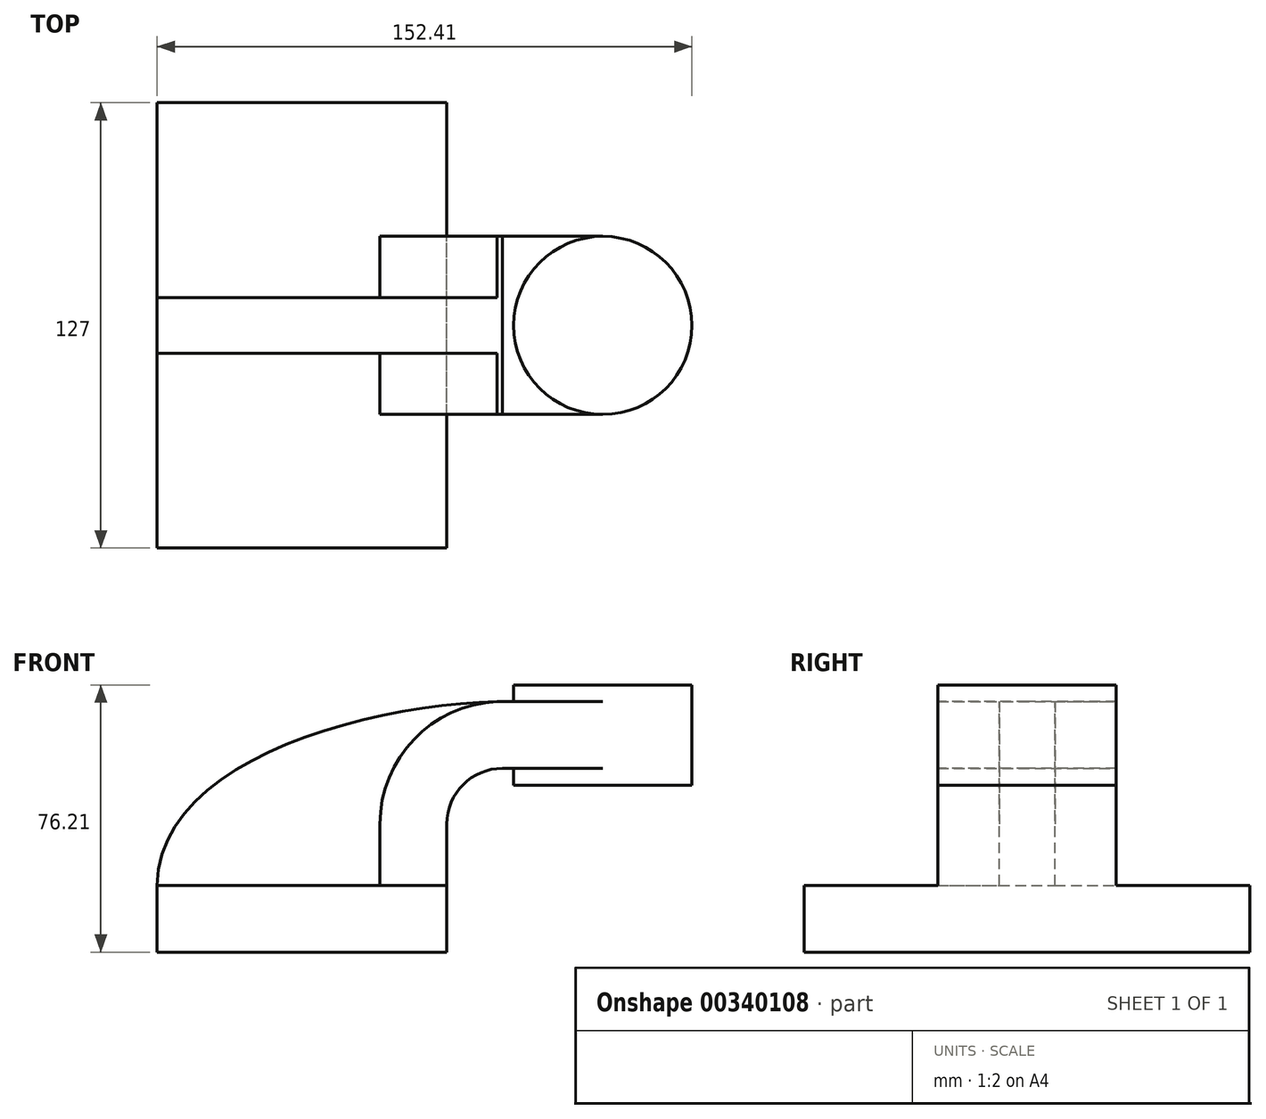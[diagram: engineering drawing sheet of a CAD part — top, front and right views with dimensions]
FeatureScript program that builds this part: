
annotation { "Feature Type Name" : "Feature", "Feature Type Description" : "" }
export const myFeature = defineFeature(function(context is Context, id is Id, definition is map)
    precondition{}
    {
        {
            var Q0;
            Q0=qCreatedBy(makeId("Front.planeOp"),FACE);
            var sketch = newSketch(context, id + "F0", { "sketchPlane" : qUnion([Q0])});
            skLineSegment(sketch, "E0.bottom", {"start": v(-41.28, -9.53) * mm, "end": v(41.28, -9.53) * mm});
            skLineSegment(sketch, "E0.top", {"start": v(-41.28, 9.52) * mm, "end": v(41.27, 9.52) * mm});
            skLineSegment(sketch, "E0.left", {"start": v(-41.27, -9.53) * mm, "end": v(-41.28, 9.52) * mm});
            skLineSegment(sketch, "E0.right", {"start": v(41.28, -9.53) * mm, "end": v(41.27, 9.52) * mm});
            skPoint(sketch, "E0.middle", {"position": v(0, 0) * mm});
            skLineSegment(sketch, "E1.bottom", {"start": v(60.32, 66.68) * mm, "end": v(111.12, 66.68) * mm});
            skLineSegment(sketch, "E1.top", {"start": v(60.32, 38.1) * mm, "end": v(111.12, 38.1) * mm});
            skLineSegment(sketch, "E1.left", {"start": v(60.32, 66.68) * mm, "end": v(60.32, 38.1) * mm});
            skLineSegment(sketch, "E1.right", {"start": v(111.12, 66.68) * mm, "end": v(111.12, 38.1) * mm});
            skPoint(sketch, "E1.middle", {"position": v(85.72, 52.39) * mm});
            skLineSegment(sketch, "E2", {"start": v(41.27, 9.52) * mm, "end": v(41.27, 27) * mm});
            skArc(sketch, "E3", {"start": v(41.27, 27) * mm, "mid": v(45.92, 38.23) * mm, "end": v(57.15, 42.88) * mm});
            skLineSegment(sketch, "E4", {"start": v(57.15, 42.88) * mm, "end": v(85.72, 42.88) * mm});
            skLineSegment(sketch, "E5.0", {"start": v(57.15, 61.93) * mm, "end": v(85.72, 61.93) * mm});
            skArc(sketch, "E5.1", {"start": v(22.22, 27) * mm, "mid": v(32.45, 51.7) * mm, "end": v(57.15, 61.93) * mm});
            skLineSegment(sketch, "E5.2", {"start": v(22.22, 9.52) * mm, "end": v(22.22, 27) * mm});
            skFitSpline(sketch, "E6", {"points": [v(-41.28, 9.53) * mm, v(57.15, 61.93) * mm], "startDerivative": vector(1.65, 107.81) * mm, "endDerivative": vector(115.03, 1.9) * mm});
            skLineSegment(sketch, "E7", {"start": v(85.72, 61.93) * mm, "end": v(85.72, 42.88) * mm});
            skLineSegment(sketch, "E8", {"start": v(85.72, 38.1) * mm, "end": v(85.72, 66.68) * mm});
            skSolve(sketch);
        }
        {
            var Q0;
            Q0=makeQuery(id+"F0.imprint","IMPRINT",FACE,{"disambiguationData":[TD([[makeQuery(id+"F0.imprint","IMPRINT",EDGE,{"derivedFrom":sQuery(id+"F0.wireOp",EDGE,"E0.bottom")}),1.0]])]});
            extrude(context, id + "F1", {"entities" : qUnion([Q0]), "endBound" : BoundingType.SYMMETRIC, "depth" : 127 * mm});
        }
        {
            var Q0;
            {var subQ0=sQuery(id+"F0.wireOp",EDGE,"E2");Q0=makeQuery(id+"F0.imprint","IMPRINT",FACE,{"disambiguationData":[TD([[makeQuery(id+"F0.imprint","IMPRINT",EDGE,{"derivedFrom":subQ0}),1.0]])]});}
            extrude(context, id + "F2", {"entities" : qUnion([Q0]), "operationType" : NewBodyOperationType.ADD, "endBound" : BoundingType.SYMMETRIC, "depth" : 50.8 * mm});
        }
        {
            var Q0;
            {var subQ0=sQuery(id+"F0.wireOp",EDGE,"E5.0");var subQ1=sQuery(id+"F0.wireOp",EDGE,"E1.left");var subQ2=makeQuery(id+"F0.imprint","INTERSECT",VERTEX,{"derivedFrom":[subQ1,subQ0]});Q0=makeQuery(id+"F0.imprint","IMPRINT",FACE,{"disambiguationData":[TD([[makeQuery(id+"F0.imprint","IMPRINT",EDGE,{"disambiguationData":[TD([[subQ2,-1.0]])],"derivedFrom":subQ1}),1.0]])]});}
            extrude(context, id + "F3", {"entities" : qUnion([Q0]), "operationType" : NewBodyOperationType.ADD, "endBound" : BoundingType.SYMMETRIC, "depth" : 50.8 * mm});
        }
        {
            var Q0;
            {var subQ3=sQuery(id+"F0.wireOp",EDGE,"E5.2");Q0=makeQuery(id+"F0.imprint","IMPRINT",FACE,{"disambiguationData":[TD([[makeQuery(id+"F0.imprint","IMPRINT",EDGE,{"derivedFrom":subQ3}),1.0]])]});}
            extrude(context, id + "F4", {"entities" : qUnion([Q0]), "operationType" : NewBodyOperationType.ADD, "endBound" : BoundingType.SYMMETRIC, "depth" : 15.88 * mm});
        }
        {
            var Q0;
            {var subQ4=sQuery(id+"F0.wireOp",EDGE,"E1.right");Q0=makeQuery(id+"F0.imprint","IMPRINT",FACE,{"disambiguationData":[TD([[makeQuery(id+"F0.imprint","IMPRINT",EDGE,{"derivedFrom":subQ4}),-1.0]])]});}
            var Q1;
            Q1=sQuery(id+"F0.wireOp",EDGE,"E8");
            revolve(context, id + "F5", {"operationType" : NewBodyOperationType.ADD, "entities" : qUnion([Q0]), "axis" : qUnion([Q1]), "revolveType" : RevolveType.FULL});
        }
    });
